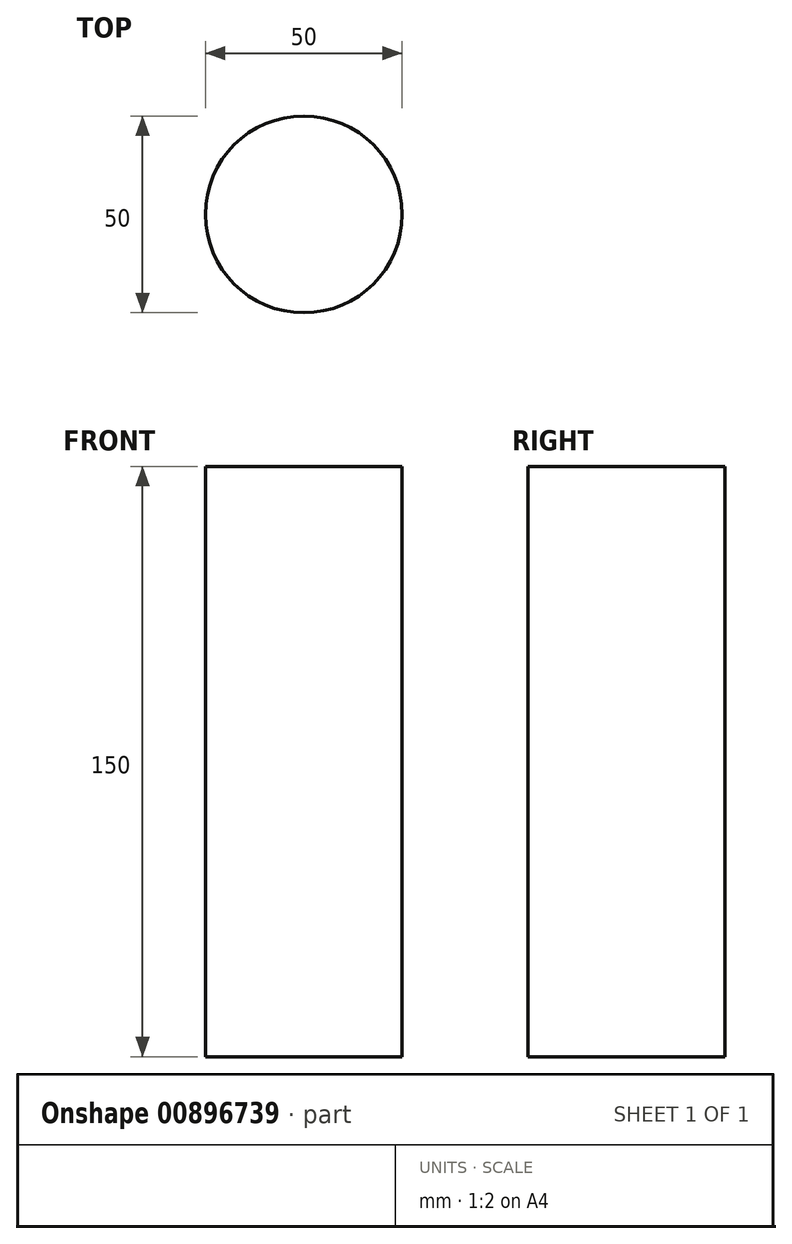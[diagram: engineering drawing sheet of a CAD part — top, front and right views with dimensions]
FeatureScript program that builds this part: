
annotation { "Feature Type Name" : "Feature", "Feature Type Description" : "" }
export const myFeature = defineFeature(function(context is Context, id is Id, definition is map)
    precondition{}
    {
        {
            var Q0;
            Q0=qCreatedBy(makeId("Top.planeOp"),FACE);
            var sketch = newSketch(context, id + "F0", { "sketchPlane" : qUnion([Q0])});
            skCircle(sketch, "E0", {"center": v(0, 0) * mm, "radius": 25 * mm});
            skSolve(sketch);
        }
        {
            var Q0;
            Q0=makeQuery(id+"F0.imprint","IMPRINT",FACE,{"disambiguationData":[TD([[makeQuery(id+"F0.imprint","IMPRINT",EDGE,{"derivedFrom":sQuery(id+"F0.wireOp",EDGE,"E0")}),1.0]])]});
            extrude(context, id + "F1", {"entities" : qUnion([Q0]), "depth" : 150 * mm, "offsetDistance" : 25 * mm});
        }
    });
